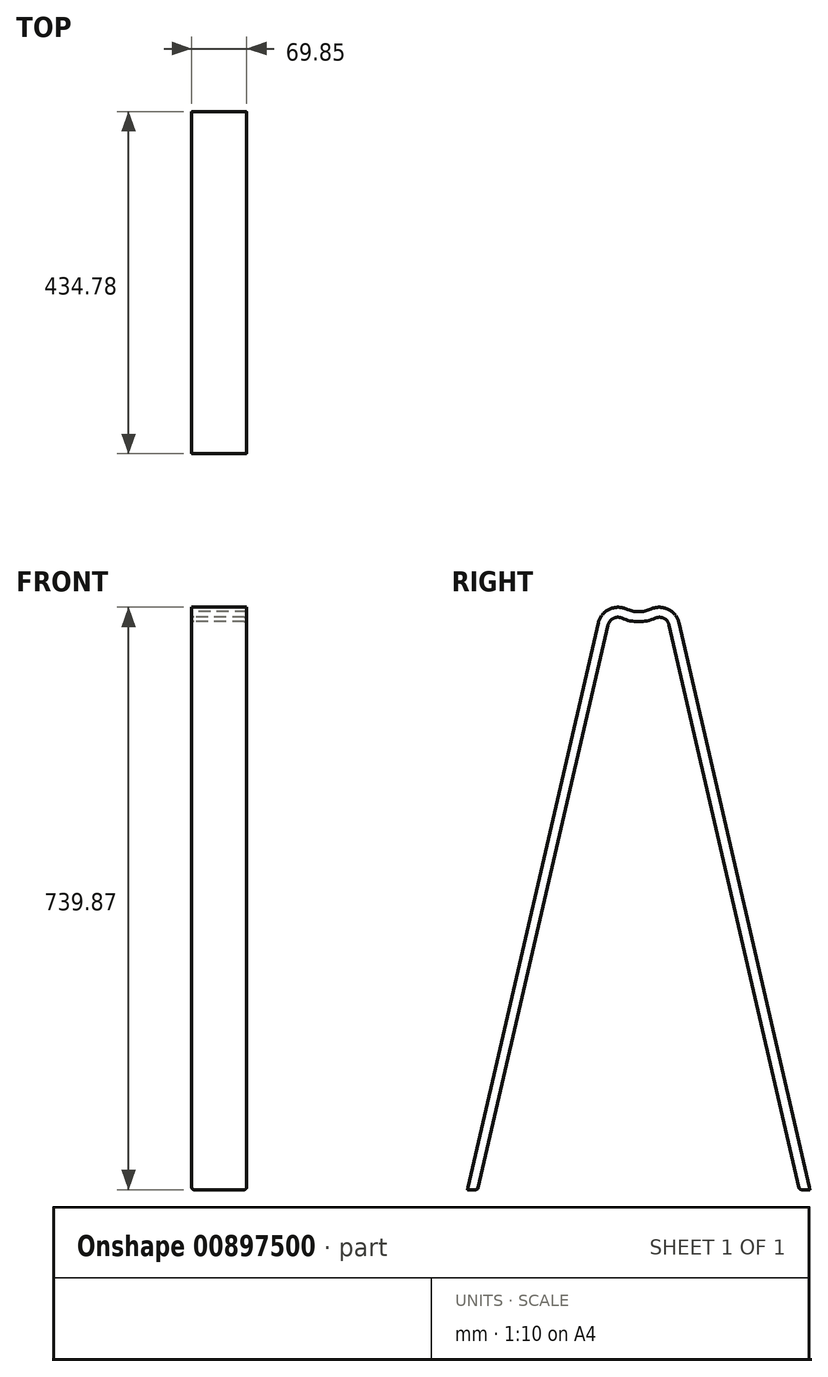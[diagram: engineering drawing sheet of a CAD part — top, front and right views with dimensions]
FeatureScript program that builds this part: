
annotation { "Feature Type Name" : "Feature", "Feature Type Description" : "" }
export const myFeature = defineFeature(function(context is Context, id is Id, definition is map)
    precondition{}
    {
        {
            var Q0;
            Q0=qCreatedBy(makeId("Right.planeOp"),FACE);
            var sketch = newSketch(context, id + "F0", { "sketchPlane" : qUnion([Q0])});
            skLineSegment(sketch, "E0", {"start": v(-24.33, 337.7) * mm, "end": v(141.94, -382.49) * mm});
            skLineSegment(sketch, "E1", {"start": v(-126.57, 337.7) * mm, "end": v(-292.84, -382.49) * mm});
            skPoint(sketch, "E2.start.orphan", {"position": v(-75.45, 446.9) * mm});
            skArc(sketch, "E3", {"start": v(-91.27, 355.09) * mm, "mid": v(-75.45, 351.65) * mm, "end": v(-59.63, 355.09) * mm});
            skArc(sketch, "E4", {"start": v(-96.54, 343.54) * mm, "mid": v(-107.43, 343.38) * mm, "end": v(-114.2, 334.84) * mm});
            skArc(sketch, "E5", {"start": v(-36.7, 334.84) * mm, "mid": v(-43.46, 343.38) * mm, "end": v(-54.35, 343.54) * mm});
            skArc(sketch, "E6.0", {"start": v(-24.33, 337.7) * mm, "mid": v(-37.85, 354.77) * mm, "end": v(-59.63, 355.09) * mm});
            skArc(sketch, "E7.0", {"start": v(-91.27, 355.09) * mm, "mid": v(-113.05, 354.77) * mm, "end": v(-126.57, 337.7) * mm});
            skLineSegment(sketch, "E8.trimOffspring", {"start": v(-114.2, 334.84) * mm, "end": v(-213.96, -97.3) * mm});
            skArc(sketch, "E9.trimOffspring", {"start": v(-96.54, 343.54) * mm, "mid": v(-75.45, 338.95) * mm, "end": v(-54.35, 343.54) * mm});
            skLineSegment(sketch, "E10.trimOffspring", {"start": v(-36.7, 334.84) * mm, "end": v(63.07, -97.3) * mm});
            skLineSegment(sketch, "E11.trimOffspring", {"start": v(-213.96, -97.3) * mm, "end": v(-279.8, -382.49) * mm});
            skLineSegment(sketch, "E12.trimOffspring", {"start": v(63.07, -97.3) * mm, "end": v(128.9, -382.49) * mm});
            skLineSegment(sketch, "E13", {"start": v(141.94, -382.49) * mm, "end": v(128.9, -382.49) * mm});
            skLineSegment(sketch, "E14", {"start": v(-292.84, -382.49) * mm, "end": v(-279.8, -382.49) * mm});
            skPoint(sketch, "E15.orphan", {"position": v(-280.7, -386.38) * mm});
            skPoint(sketch, "E16.orphan", {"position": v(129.98, -387.13) * mm});
            skPoint(sketch, "E17.center.orphan", {"position": v(-75.45, 46.38) * mm});
            skSolve(sketch);
        }
        {
            var Q0;
            Q0=makeQuery(id+"F0.imprint","IMPRINT",FACE,{"disambiguationData":[TD([[makeQuery(id+"F0.imprint","IMPRINT",EDGE,{"derivedFrom":sQuery(id+"F0.wireOp",EDGE,"E0")}),-1.0]])]});
            extrude(context, id + "F1", {"entities" : qUnion([Q0]), "depth" : 69.85 * mm, "offsetDistance" : 25.4 * mm});
        }
        {
            var Q0;
            Q0=makeQuery(id+"F1.opExtrude","SWEPT_FACE",FACE,{"disambiguationData":[OSD([sQuery(id+"F0.wireOp",EDGE,"E10.trimOffspring"),sQuery(id+"F0.wireOp",EDGE,"E12.trimOffspring")])]});
            var Q1;
            Q1=makeQuery(id+"F1.opExtrude","SWEPT_EDGE",EDGE,{"disambiguationData":[OSD([sQuery(id+"F0.wireOp",EDGE,"E11.trimOffspring"),sQuery(id+"F0.wireOp",EDGE,"E14")])]});
            fillet(context, id + "F2", {"entities" : qUnion([Q0, Q1]), "radius" : 3.17 * mm, "tangentPropagation" : true, "allowEdgeOverflow" : false});
        }
        {
            var Q0;
            Q0=makeQuery(id+"F1.opExtrude","CAP_EDGE",EDGE,{"disambiguationData":[OSD([sQuery(id+"F0.wireOp",EDGE,"E13")])],"isStart":true});
            var Q1;
            Q1=makeQuery(id+"F1.opExtrude","CAP_EDGE",EDGE,{"disambiguationData":[OSD([sQuery(id+"F0.wireOp",EDGE,"E13")])],"isStart":false});
            var Q2;
            Q2=makeQuery(id+"F1.opExtrude","CAP_EDGE",EDGE,{"disambiguationData":[OSD([sQuery(id+"F0.wireOp",EDGE,"E14")])],"isStart":true});
            var Q3;
            Q3=makeQuery(id+"F1.opExtrude","CAP_EDGE",EDGE,{"disambiguationData":[OSD([sQuery(id+"F0.wireOp",EDGE,"E14")])],"isStart":false});
            fillet(context, id + "F3", {"entities" : qUnion([Q0, Q1, Q2, Q3]), "radius" : 3.17 * mm, "tangentPropagation" : true, "allowEdgeOverflow" : false});
        }
    });
